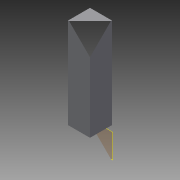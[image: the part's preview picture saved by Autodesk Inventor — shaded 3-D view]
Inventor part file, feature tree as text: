
AUTODESK INVENTOR PART (.ipt)
format: ipt  version: 2015 (Build 190159000, 159)  size: 68,608 bytes
history: native  units: in
note: dims shown in document units (in); Inventor stores cm internally (conversion verified against a paired STEP export)
features: reference x2, plane x1, extrude x1, sketch x1
ambient origin geometry x8: Origin, YZ Plane, XZ Plane, XY Plane, X Axis, Y Axis, Z Axis, Center Point
bodies: Solid1 (feature_tree)
feature tree (5):
  plane  "Work Plane1"
  extrude  "Extrusion1"  [1 undecoded]
  sketch  "Sketch1"  dims[d0=0.75in d1=0.0in]
  reference  "Reference1"
  reference  "Reference2"
note: 1 required parameter value undecoded (feature->parameter linkage not recoverable at this tier; creation-order binding heuristic only, values carry confidence <= 0.55)
